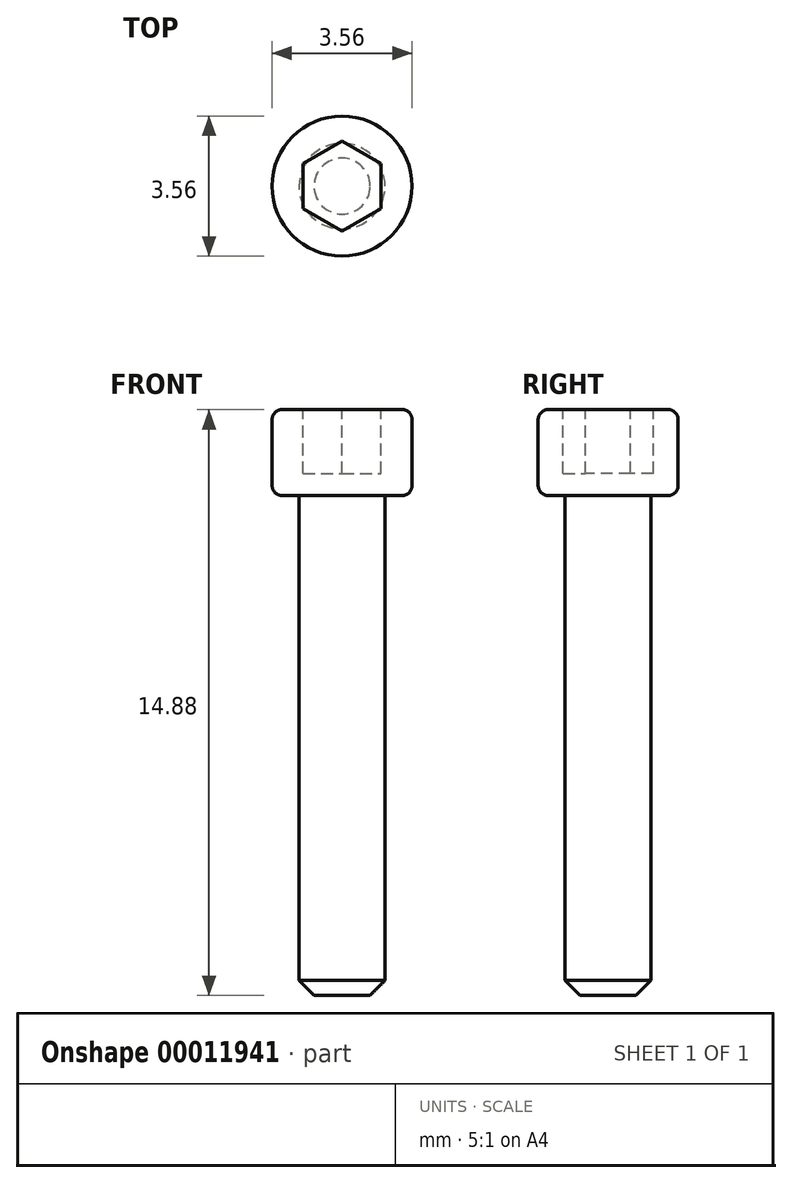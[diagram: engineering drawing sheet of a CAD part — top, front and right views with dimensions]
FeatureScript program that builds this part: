
annotation { "Feature Type Name" : "Feature", "Feature Type Description" : "" }
export const myFeature = defineFeature(function(context is Context, id is Id, definition is map)
    precondition{}
    {
        {
            var Q0;
            Q0=qCreatedBy(makeId("Top.planeOp"),FACE);
            var sketch = newSketch(context, id + "F0", { "sketchPlane" : qUnion([Q0]), "disableImprinting" : false});
            skCircle(sketch, "E0", {"center": v(0, 0) * mm, "radius": 1.1 * mm});
            skSolve(sketch);
        }
        {
            var Q0;
            Q0=makeQuery(id+"F0.imprint","IMPRINT",FACE,{"disambiguationData":[TD([[makeQuery(id+"F0.imprint","IMPRINT",EDGE,{"derivedFrom":sQuery(id+"F0.wireOp",EDGE,"E0")}),1.0]])]});
            extrude(context, id + "F1", {"entities" : qUnion([Q0]), "oppositeDirection" : true, "depth" : 12.7 * mm});
        }
        {
            var Q0;
            Q0=qCreatedBy(makeId("Top.planeOp"),FACE);
            var sketch = newSketch(context, id + "F2", { "sketchPlane" : qUnion([Q0])});
            skCircle(sketch, "E1", {"center": v(0, 0) * mm, "radius": 1.78 * mm});
            skSolve(sketch);
        }
        {
            var Q0;
            Q0=qSketchRegion(id+"F2",true);
            extrude(context, id + "F3", {"entities" : qUnion([Q0]), "operationType" : NewBodyOperationType.ADD, "depth" : 2.18 * mm});
        }
        {
            var Q0;
            Q0=makeQuery(id+"F3.opExtrude","CAP_FACE",FACE,{"disambiguationData":[OSD([sQuery(id+"F2.wireOp",EDGE,"E1")])],"isStart":false});
            var sketch = newSketch(context, id + "F4", { "sketchPlane" : qUnion([Q0])});
            skCircle(sketch, "E2.cCircle", {"center": v(0, 0) * mm, "radius": 1 * mm, "construction": true});
            skLineSegment(sketch, "E2.0", {"start": v(1, 0.57) * mm, "end": v(1, -0.57) * mm});
            skLineSegment(sketch, "E2.1", {"start": v(1, -0.57) * mm, "end": v(0, -1.15) * mm});
            skLineSegment(sketch, "E2.2", {"start": v(0, -1.15) * mm, "end": v(-1, -0.57) * mm});
            skLineSegment(sketch, "E2.3", {"start": v(-1, -0.57) * mm, "end": v(-1, 0.57) * mm});
            skLineSegment(sketch, "E2.4", {"start": v(-1, 0.57) * mm, "end": v(0, 1.15) * mm});
            skLineSegment(sketch, "E2.5", {"start": v(0, 1.15) * mm, "end": v(1, 0.57) * mm});
            skPoint(sketch, "E2.0.midPoint", {"position": v(1, 0) * mm});
            skSolve(sketch);
        }
        {
            var Q0;
            Q0=makeQuery(id+"F4.imprint","IMPRINT",FACE,{"disambiguationData":[TD([[makeQuery(id+"F4.imprint","IMPRINT",EDGE,{"derivedFrom":sQuery(id+"F4.wireOp",EDGE,"E2.0")}),-1.0]])]});
            extrude(context, id + "F5", {"entities" : qUnion([Q0]), "operationType" : NewBodyOperationType.REMOVE, "flatOperationType" : FlatOperationType.REMOVE, "oppositeDirection" : true, "depth" : 1.63 * mm, "offsetDistance" : 25.4 * mm, "domain" : OperationDomain.MODEL});
        }
        {
            var Q0;
            Q0=makeQuery(id+"F1.opExtrude","CAP_EDGE",EDGE,{"disambiguationData":[OSD([sQuery(id+"F0.wireOp",EDGE,"E0")])],"isStart":false});
            chamfer(context, id + "F6", {"entities" : qUnion([Q0]), "chamferType" : ChamferType.OFFSET_ANGLE, "width" : 0.38 * mm, "oppositeDirection" : false, "angle" : 45 * degree, "tangentPropagation" : true});
        }
        {
            var Q0;
            Q0=qCreatedBy(makeId("Top.planeOp"),FACE);
            cPlane(context, id + "F7", {"entities" : qUnion([Q0]), "cplaneType" : CPlaneType.OFFSET, "offset" : ((1 / 56) * 2) * mm, "oppositeDirection" : true, "width" : 152.4 * mm, "height" : 152.4 * mm});
        }
        {
            var Q0;
            Q0=qCreatedBy(id+"F7.planeOp",FACE);
            var sketch = newSketch(context, id + "F8", { "sketchPlane" : qUnion([Q0])});
            skCircle(sketch, "E3", {"center": v(0, 0) * mm, "radius": 0.8 * mm});
            skSolve(sketch);
        }
        {
            var Q0;
            Q0=sQuery(id+"F8.wireOp",EDGE,"E3");
            var Q1;
            Q1=makeQuery(id+"F6.opChamfer","BLEND_FACE",FACE,{"disambiguationData":[OSD([sQuery(id+"F0.wireOp",EDGE,"E0")])]});
            extrude(context, id + "F9", {"bodyType" : ToolBodyType.SURFACE, "surfaceEntities" : qUnion([Q0]), "endBound" : BoundingType.UP_TO_SURFACE, "oppositeDirection" : true, "endBoundEntityFace" : qUnion([Q1]), "depth" : 25.4 * mm});
        }
        {
            var Q0;
            Q0=makeQuery(id+"F3.opExtrude","CAP_EDGE",EDGE,{"disambiguationData":[OSD([sQuery(id+"F2.wireOp",EDGE,"E1")])],"isStart":false});
            var Q1;
            Q1=makeQuery(id+"F3.opExtrude","CAP_EDGE",EDGE,{"disambiguationData":[OSD([sQuery(id+"F2.wireOp",EDGE,"E1")])],"isStart":true});
            fillet(context, id + "F10", {"entities" : qUnion([Q0, Q1]), "radius" : 0.25 * mm, "tangentPropagation" : true, "allowEdgeOverflow" : false});
        }
    });
